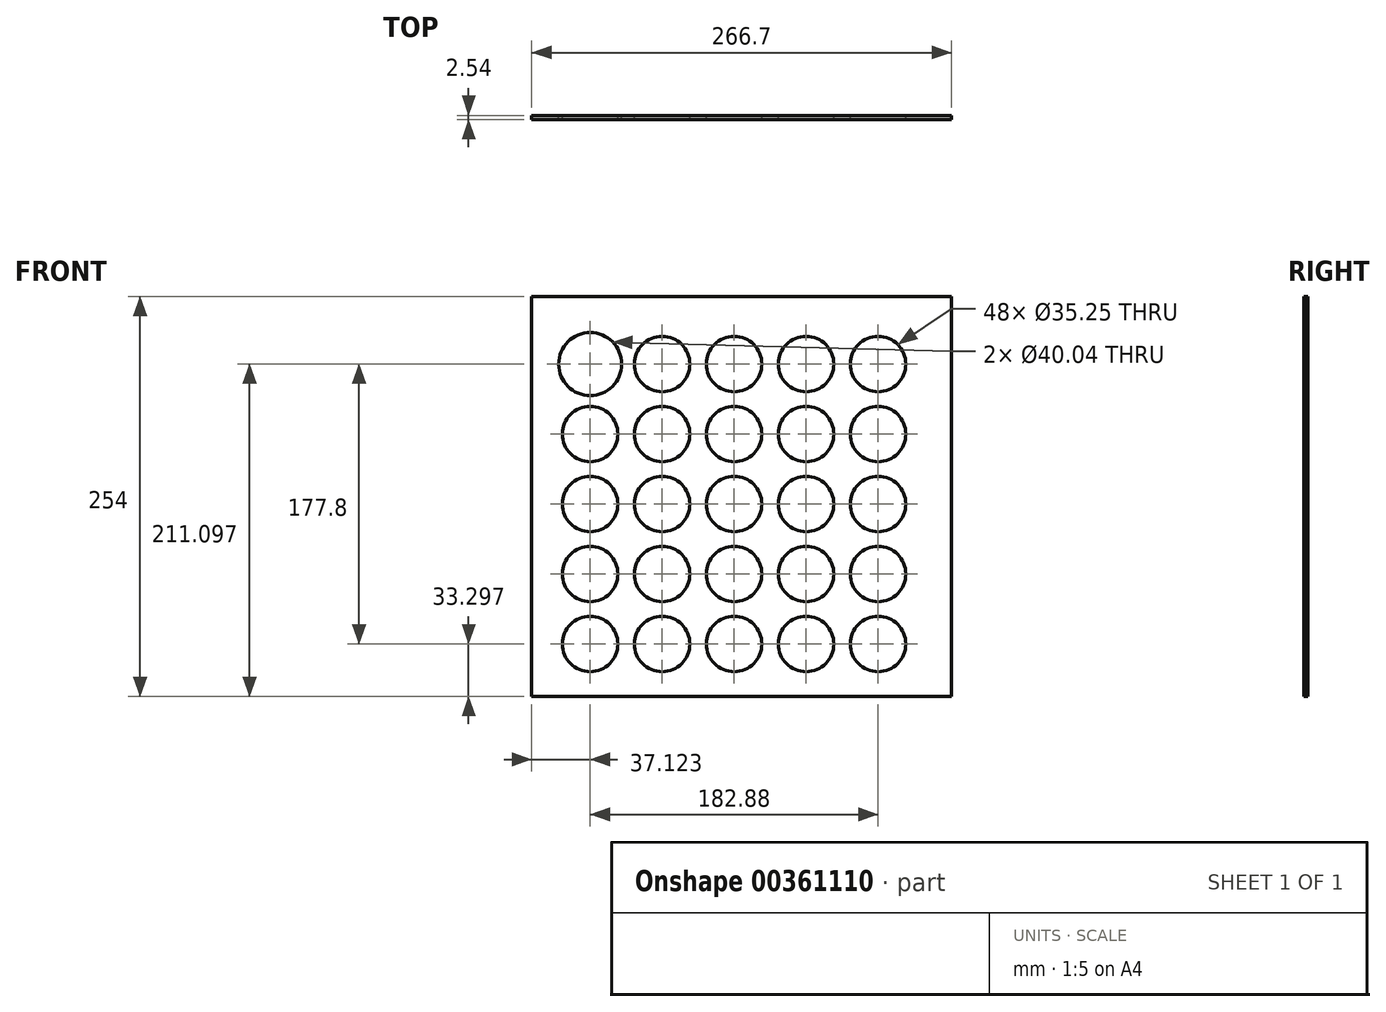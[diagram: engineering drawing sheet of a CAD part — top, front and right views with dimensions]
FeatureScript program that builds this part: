
annotation { "Feature Type Name" : "Feature", "Feature Type Description" : "" }
export const myFeature = defineFeature(function(context is Context, id is Id, definition is map)
    precondition{}
    {
        {
            var Q0;
            Q0=qCreatedBy(makeId("Front.planeOp"),FACE);
            var sketch = newSketch(context, id + "F0", { "sketchPlane" : qUnion([Q0])});
            skLineSegment(sketch, "E0.bottom", {"start": v(-105.95, 167.4) * mm, "end": v(160.75, 167.4) * mm});
            skLineSegment(sketch, "E0.top", {"start": v(-105.95, -86.6) * mm, "end": v(160.75, -86.6) * mm});
            skLineSegment(sketch, "E0.left", {"start": v(-105.95, 167.4) * mm, "end": v(-105.95, -86.6) * mm});
            skLineSegment(sketch, "E0.right", {"start": v(160.75, 167.4) * mm, "end": v(160.75, -86.6) * mm});
            skCircle(sketch, "E1", {"center": v(-68.83, 124.5) * mm, "radius": 20.02 * mm});
            skCircle(sketch, "E2", {"center": v(-68.83, 124.5) * mm, "radius": 17.62 * mm});
            skCircle(sketch, "E3.0.1.0", {"center": v(-68.83, 80.06) * mm, "radius": 17.62 * mm});
            skCircle(sketch, "E3.0.2.0", {"center": v(-68.83, 35.6) * mm, "radius": 17.62 * mm});
            skCircle(sketch, "E3.0.3.0", {"center": v(-68.83, -8.84) * mm, "radius": 17.62 * mm});
            skCircle(sketch, "E3.0.4.0", {"center": v(-68.83, -53.3) * mm, "radius": 17.62 * mm});
            skCircle(sketch, "E3.1.0.0", {"center": v(-23.1, 124.5) * mm, "radius": 17.62 * mm});
            skCircle(sketch, "E3.1.1.0", {"center": v(-23.1, 80.06) * mm, "radius": 17.62 * mm});
            skCircle(sketch, "E3.1.2.0", {"center": v(-23.1, 35.6) * mm, "radius": 17.62 * mm});
            skCircle(sketch, "E3.1.3.0", {"center": v(-23.1, -8.84) * mm, "radius": 17.62 * mm});
            skCircle(sketch, "E3.1.4.0", {"center": v(-23.1, -53.3) * mm, "radius": 17.62 * mm});
            skCircle(sketch, "E3.2.0.0", {"center": v(22.61, 124.5) * mm, "radius": 17.62 * mm});
            skCircle(sketch, "E3.2.1.0", {"center": v(22.61, 80.06) * mm, "radius": 17.62 * mm});
            skCircle(sketch, "E3.2.2.0", {"center": v(22.61, 35.6) * mm, "radius": 17.62 * mm});
            skCircle(sketch, "E3.2.3.0", {"center": v(22.61, -8.84) * mm, "radius": 17.62 * mm});
            skCircle(sketch, "E3.2.4.0", {"center": v(22.61, -53.3) * mm, "radius": 17.62 * mm});
            skCircle(sketch, "E3.3.0.0", {"center": v(68.33, 124.5) * mm, "radius": 17.62 * mm});
            skCircle(sketch, "E3.3.1.0", {"center": v(68.33, 80.06) * mm, "radius": 17.62 * mm});
            skCircle(sketch, "E3.3.2.0", {"center": v(68.33, 35.6) * mm, "radius": 17.62 * mm});
            skCircle(sketch, "E3.3.3.0", {"center": v(68.33, -8.84) * mm, "radius": 17.62 * mm});
            skCircle(sketch, "E3.3.4.0", {"center": v(68.33, -53.3) * mm, "radius": 17.62 * mm});
            skCircle(sketch, "E3.4.0.0", {"center": v(114.05, 124.5) * mm, "radius": 17.62 * mm});
            skCircle(sketch, "E3.4.1.0", {"center": v(114.05, 80.06) * mm, "radius": 17.62 * mm});
            skCircle(sketch, "E3.4.2.0", {"center": v(114.05, 35.6) * mm, "radius": 17.62 * mm});
            skCircle(sketch, "E3.4.3.0", {"center": v(114.05, -8.84) * mm, "radius": 17.62 * mm});
            skCircle(sketch, "E3.4.4.0", {"center": v(114.05, -53.3) * mm, "radius": 17.62 * mm});
            skLineSegment(sketch, "E3.direction1", {"start": v(-68.83, 124.5) * mm, "end": v(-23.1, 124.5) * mm, "construction": true});
            skLineSegment(sketch, "E3.direction2", {"start": v(-68.83, 124.5) * mm, "end": v(-68.83, 80.06) * mm, "construction": true});
            skSolve(sketch);
        }
        {
            var Q0;
            Q0=qSketchRegion(id+"F0",true);
            extrude(context, id + "F1", {"entities" : qUnion([Q0]), "depth" : 2.54 * mm});
        }
        {
            var Q0;
            Q0=qSketchRegion(id+"F0",true);
            extrude(context, id + "F2", {"entities" : qUnion([Q0]), "operationType" : NewBodyOperationType.ADD, "depth" : 1.27 * mm});
        }
        {
            var Q0;
            Q0=makeQuery(id+"F0.imprint","IMPRINT",FACE,{"disambiguationData":[TD([[makeQuery(id+"F0.imprint","IMPRINT",EDGE,{"derivedFrom":sQuery(id+"F0.wireOp",EDGE,"E0.bottom")}),-1.0]])]});
            extrude(context, id + "F3", {"entities" : qUnion([Q0]), "depth" : 0.25 * mm});
        }
    });
